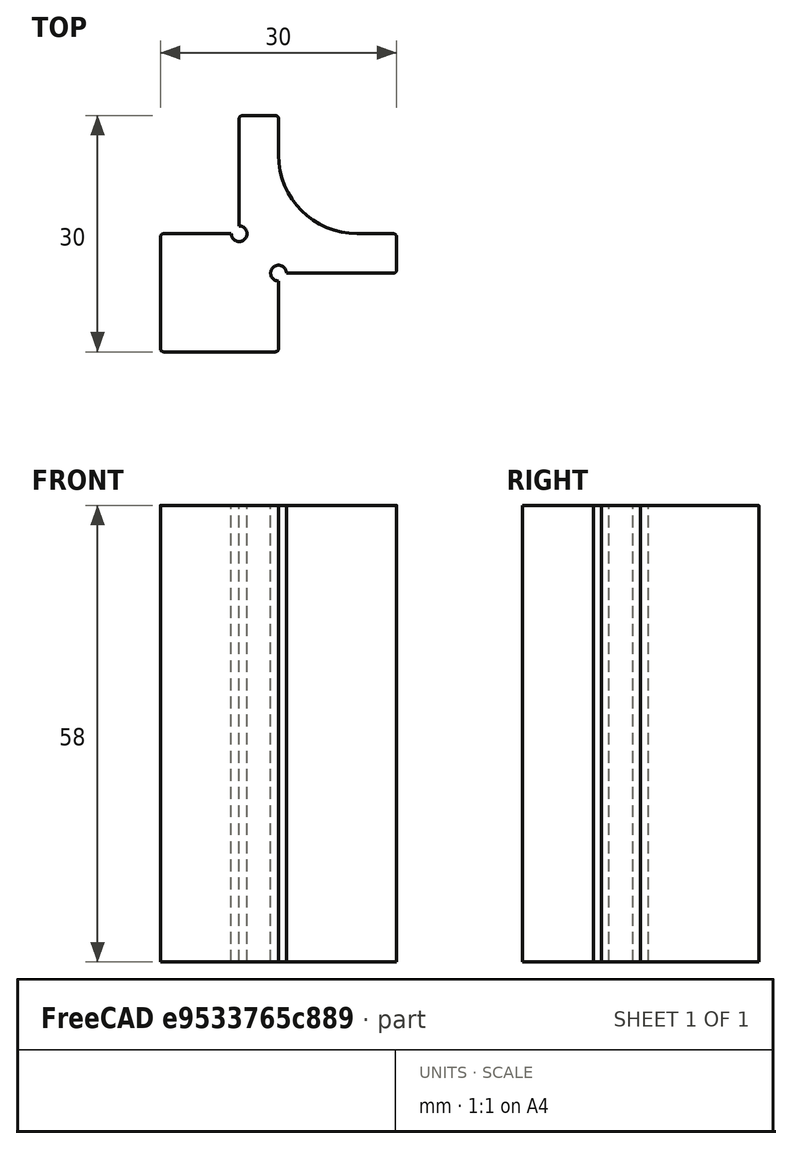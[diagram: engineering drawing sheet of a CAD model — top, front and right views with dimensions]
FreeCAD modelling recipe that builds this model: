
FCSTD DOCUMENT  (FreeCAD 0.18R16146 (Git))
Label: EckstückVakumtisch
License: All rights reserved
LicenseURL: http://en.wikipedia.org/wiki/All_rights_reserved
objects: Part::Cut×5, Part::Box×4, Part::Fillet×2, Part::Cylinder×2
note: 13 computed .brp shape members not serialized (recipe doc carries the construction recipe); baked Part::Feature solids carry a one-line shape summary decoded from their .brp

FEATURE [Part::Box] Box  label="Cube"
  AttacherType = Attacher::AttachEngine3D
  Height = 58
  Length = 30
  Width = 30
FEATURE [Part::Box] Box001  label="Cube001"
  AttacherType = Attacher::AttachEngine3D
  Height = 58
  Length = 15
  Placement = pos=(15,0,0) rot=(0,0,1;0rad)
  Width = 10
FEATURE [Part::Box] Box002  label="Cube002"
  AttacherType = Attacher::AttachEngine3D
  Height = 58
  Length = 10
  Placement = pos=(0,15,0) rot=(0,0,1;0rad)
  Width = 15
FEATURE [Part::Box] Box003  label="Cube003"
  AttacherType = Attacher::AttachEngine3D
  Height = 58
  Length = 15
  Placement = pos=(15,15,0) rot=(0,0,1;0rad)
  Width = 15
FEATURE [Part::Fillet] Fillet
  Base = -> Box003
  Edges = 1 edges r=10: [Edge1]
FEATURE [Part::Cylinder] Cylinder
  Angle = 360
  AttacherType = Attacher::AttachEngine3D
  Height = 58
  Placement = pos=(15,10,0) rot=(0,0,1;0rad)
  Radius = 1
FEATURE [Part::Cylinder] Cylinder001
  Angle = 360
  AttacherType = Attacher::AttachEngine3D
  Height = 58
  Placement = pos=(10,15,0) rot=(0,0,1;0rad)
  Radius = 1
FEATURE [Part::Cut] Cut
  Base = -> Box
  Tool = -> Box001
FEATURE [Part::Cut] Cut001
  Base = -> Cut
  Tool = -> Box002
FEATURE [Part::Cut] Cut002
  Base = -> Cut001
  Tool = -> Cylinder001
FEATURE [Part::Cut] Cut003
  Base = -> Cut002
  Tool = -> Cylinder
FEATURE [Part::Cut] Cut004
  Base = -> Cut003
  Tool = -> Fillet
FEATURE [Part::Fillet] Fillet001
  Base = -> Cut004
  Edges = 7 edges r=0.4: [Edge2,Edge4,Edge32,Edge33,Edge34,Edge37,Edge38]
